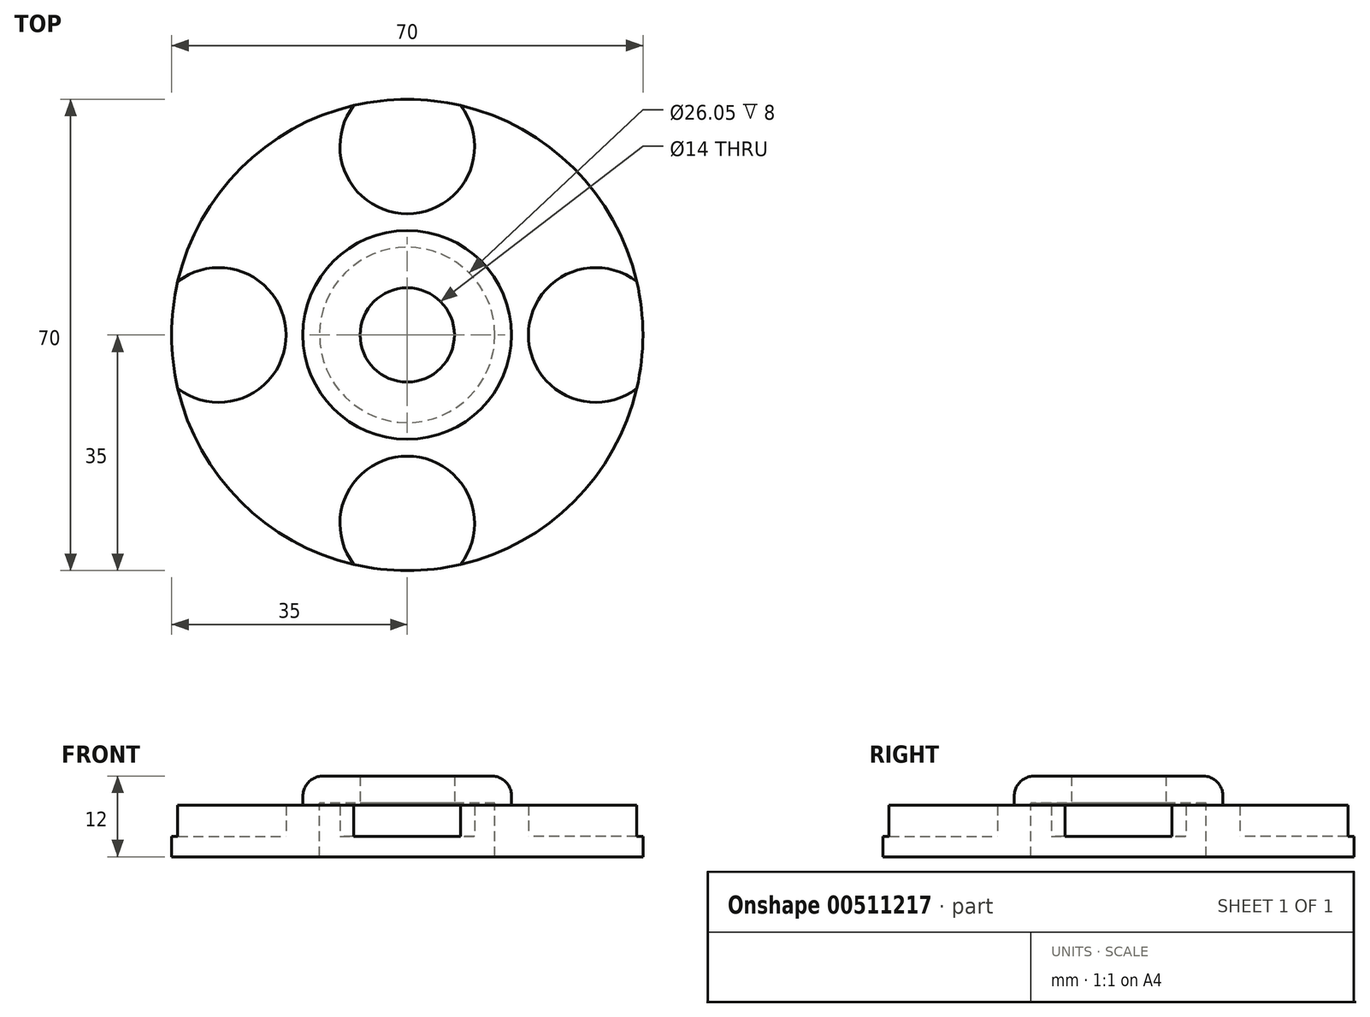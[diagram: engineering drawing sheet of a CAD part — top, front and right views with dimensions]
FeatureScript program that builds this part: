
annotation { "Feature Type Name" : "Feature", "Feature Type Description" : "" }
export const myFeature = defineFeature(function(context is Context, id is Id, definition is map)
    precondition{}
    {
        {
            var Q0;
            Q0=qCreatedBy(makeId("Top.planeOp"),FACE);
            var sketch = newSketch(context, id + "F0", { "sketchPlane" : qUnion([Q0])});
            skCircle(sketch, "E0", {"center": v(0, 0) * mm, "radius": 35 * mm});
            skArc(sketch, "E1", {"start": v(-7.93, 34.09) * mm, "mid": v(0, 18) * mm, "end": v(7.93, 34.09) * mm});
            skArc(sketch, "E2.1.0", {"start": v(-34.09, -7.93) * mm, "mid": v(-18, 0) * mm, "end": v(-34.09, 7.93) * mm});
            skArc(sketch, "E2.2.0", {"start": v(7.93, -34.09) * mm, "mid": v(0, -18) * mm, "end": v(-7.93, -34.09) * mm});
            skArc(sketch, "E3.1.3.0", {"start": v(34.09, 7.93) * mm, "mid": v(18, 0) * mm, "end": v(34.09, -7.93) * mm});
            skCircle(sketch, "E4", {"center": v(0, 0) * mm, "radius": 7 * mm});
            skCircle(sketch, "E5", {"center": v(0, 0) * mm, "radius": 13.03 * mm});
            skCircle(sketch, "E6", {"center": v(0, 0) * mm, "radius": 15.5 * mm});
            skSolve(sketch);
        }
        {
            var Q0;
            Q0=makeQuery(id+"F0.imprint","IMPRINT",FACE,{"disambiguationData":[TD([[makeQuery(id+"F0.imprint","IMPRINT",EDGE,{"derivedFrom":sQuery(id+"F0.wireOp",EDGE,"E0")}),1.0]])]});
            extrude(context, id + "F1", {"entities" : qUnion([Q0]), "depth" : 4.65 * mm});
        }
        {
            var Q0;
            Q0=makeQuery(id+"F0.imprint","IMPRINT",FACE,{"disambiguationData":[TD([[makeQuery(id+"F0.imprint","IMPRINT",EDGE,{"derivedFrom":sQuery(id+"F0.wireOp",EDGE,"E3.1.3.0")}),1.0]])]});
            var Q1;
            Q1=makeQuery(id+"F0.imprint","IMPRINT",FACE,{"disambiguationData":[TD([[makeQuery(id+"F0.imprint","IMPRINT",EDGE,{"derivedFrom":sQuery(id+"F0.wireOp",EDGE,"E0")}),1.0]])]});
            var Q2;
            Q2=makeQuery(id+"F0.imprint","IMPRINT",FACE,{"disambiguationData":[TD([[makeQuery(id+"F0.imprint","IMPRINT",EDGE,{"derivedFrom":sQuery(id+"F0.wireOp",EDGE,"E3.1.4.0")}),1.0]])]});
            var Q3;
            Q3=makeQuery(id+"F0.imprint","IMPRINT",FACE,{"disambiguationData":[TD([[makeQuery(id+"F0.imprint","IMPRINT",EDGE,{"derivedFrom":sQuery(id+"F0.wireOp",EDGE,"320b826b-5726-420b-8643-92be84a25810.1.5.0")}),1.0]])]});
            var Q4;
            Q4=makeQuery(id+"F0.imprint","IMPRINT",FACE,{"disambiguationData":[TD([[makeQuery(id+"F0.imprint","IMPRINT",EDGE,{"derivedFrom":sQuery(id+"F0.wireOp",EDGE,"E1")}),1.0]])]});
            var Q5;
            Q5=makeQuery(id+"F0.imprint","IMPRINT",FACE,{"disambiguationData":[TD([[makeQuery(id+"F0.imprint","IMPRINT",EDGE,{"derivedFrom":sQuery(id+"F0.wireOp",EDGE,"E2.1.0")}),1.0]])]});
            var Q6;
            Q6=makeQuery(id+"F0.imprint","IMPRINT",FACE,{"disambiguationData":[TD([[makeQuery(id+"F0.imprint","IMPRINT",EDGE,{"derivedFrom":sQuery(id+"F0.wireOp",EDGE,"E2.2.0")}),1.0]])]});
            var Q7;
            Q7=makeQuery(id+"F0.imprint","IMPRINT",FACE,{"disambiguationData":[TD([[makeQuery(id+"F0.imprint","IMPRINT",EDGE,{"derivedFrom":sQuery(id+"F0.wireOp",EDGE,"E5")}),-1.0]])]});
            extrude(context, id + "F2", {"entities" : qUnion([Q0, Q1, Q2, Q3, Q4, Q5, Q6, Q7]), "operationType" : NewBodyOperationType.ADD, "oppositeDirection" : true, "depth" : 3 * mm});
        }
        {
            var Q0;
            Q0=makeQuery(id+"F0.imprint","IMPRINT",FACE,{"disambiguationData":[TD([[makeQuery(id+"F0.imprint","IMPRINT",EDGE,{"derivedFrom":sQuery(id+"F0.wireOp",EDGE,"E5")}),-1.0]])]});
            var Q1;
            Q1=makeQuery(id+"F1.opExtrude","CAP_FACE",FACE,{"disambiguationData":[OSD([sQuery(id+"F0.wireOp",EDGE,"E4"),sQuery(id+"F0.wireOp",EDGE,"E5")])],"isStart":false});
            var Q2;
            Q2=makeQuery(id+"F0.imprint","IMPRINT",FACE,{"disambiguationData":[TD([[makeQuery(id+"F0.imprint","IMPRINT",EDGE,{"derivedFrom":sQuery(id+"F0.wireOp",EDGE,"E4")}),-1.0]])]});
            extrude(context, id + "F3", {"entities" : qUnion([Q0, Q1, Q2]), "operationType" : NewBodyOperationType.ADD, "depth" : 9 * mm});
        }
        {
            var Q0;
            Q0=makeQuery(id+"F0.imprint","IMPRINT",FACE,{"disambiguationData":[TD([[makeQuery(id+"F0.imprint","IMPRINT",EDGE,{"derivedFrom":sQuery(id+"F0.wireOp",EDGE,"E4")}),-1.0]])]});
            extrude(context, id + "F4", {"entities" : qUnion([Q0]), "operationType" : NewBodyOperationType.REMOVE, "depth" : 5 * mm});
        }
        {
            var Q0;
            Q0=makeQuery(id+"F3.opExtrude","CAP_EDGE",EDGE,{"disambiguationData":[OSD([sQuery(id+"F0.wireOp",EDGE,"E6")])],"isStart":false});
            fillet(context, id + "F5", {"entities" : qUnion([Q0]), "radius" : 3 * mm, "tangentPropagation" : true, "allowEdgeOverflow" : false});
        }
    });
